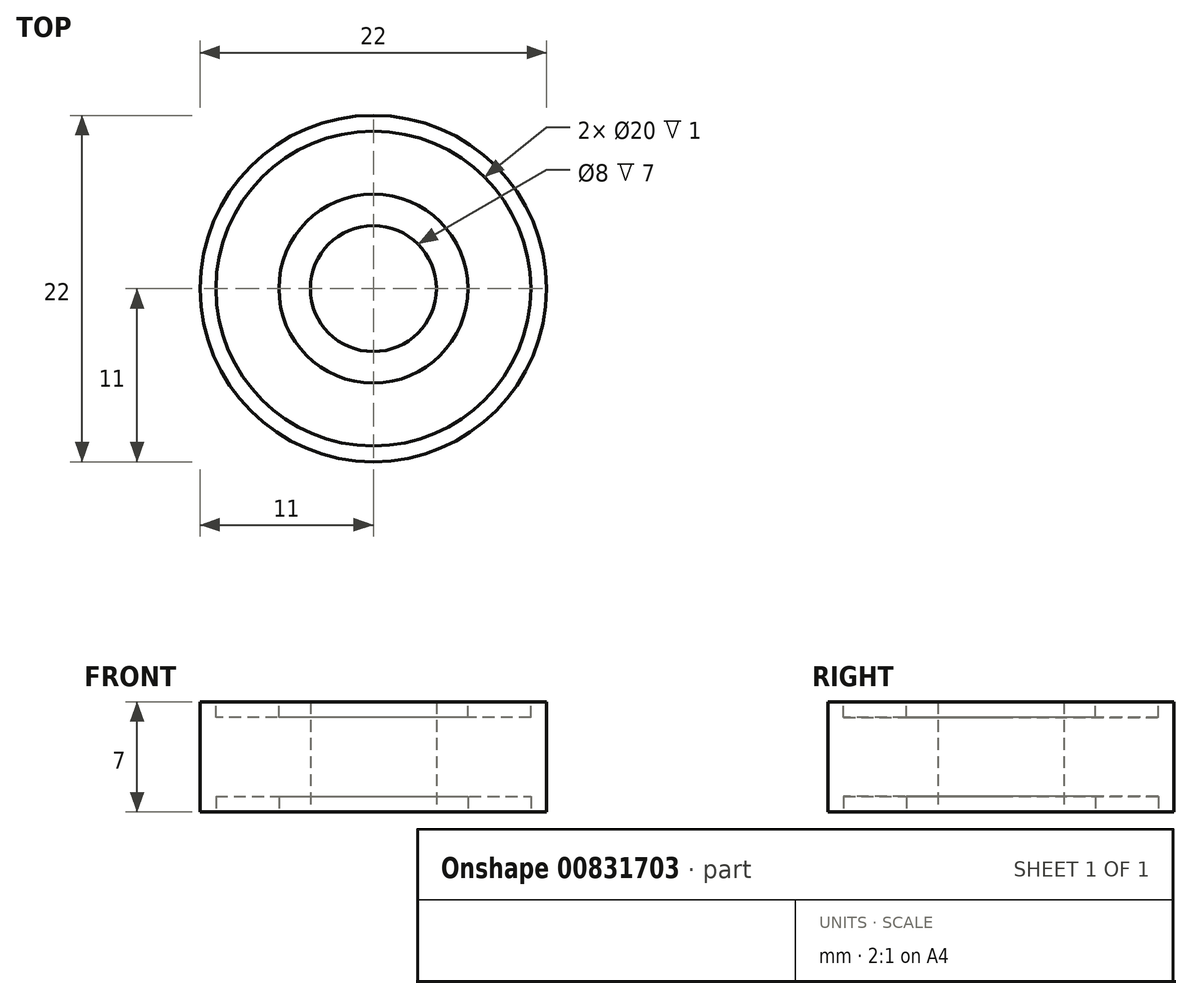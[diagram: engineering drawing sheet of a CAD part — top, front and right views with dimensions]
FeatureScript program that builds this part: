
annotation { "Feature Type Name" : "Feature", "Feature Type Description" : "" }
export const myFeature = defineFeature(function(context is Context, id is Id, definition is map)
    precondition{}
    {
        {
            var Q0;
            Q0=qCreatedBy(makeId("Top.planeOp"),FACE);
            var sketch = newSketch(context, id + "F0", { "sketchPlane" : qUnion([Q0])});
            skCircle(sketch, "E0", {"center": v(0, 0) * mm, "radius": 11 * mm});
            skCircle(sketch, "E1", {"center": v(0, 0) * mm, "radius": 4 * mm});
            skSolve(sketch);
        }
        {
            var Q0;
            Q0=makeQuery(id+"F0.imprint","IMPRINT",FACE,{"disambiguationData":[TD([[makeQuery(id+"F0.imprint","IMPRINT",EDGE,{"derivedFrom":sQuery(id+"F0.wireOp",EDGE,"E0")}),1.0]])]});
            extrude(context, id + "F1", {"entities" : qUnion([Q0]), "depth" : 7 * mm, "offsetDistance" : 25 * mm});
        }
        {
            var Q0;
            Q0=makeQuery(id+"F1.opExtrude","CAP_FACE",FACE,{"disambiguationData":[OSD([sQuery(id+"F0.wireOp",EDGE,"E0"),sQuery(id+"F0.wireOp",EDGE,"E1")])],"isStart":false});
            var sketch = newSketch(context, id + "F2", { "sketchPlane" : qUnion([Q0])});
            skLineSegment(sketch, "E2", {"start": v(-4, 0) * mm, "end": v(-11, 0) * mm});
            skLineSegment(sketch, "E3", {"start": v(4, 0) * mm, "end": v(11, 0) * mm});
            skSolve(sketch);
        }
        {
            var Q0;
            Q0=makeQuery(id+"F1.opExtrude","CAP_FACE",FACE,{"disambiguationData":[OSD([sQuery(id+"F0.wireOp",EDGE,"E0"),sQuery(id+"F0.wireOp",EDGE,"E1")])],"isStart":true});
            var sketch = newSketch(context, id + "F3", { "sketchPlane" : qUnion([Q0])});
            skLineSegment(sketch, "E4", {"start": v(-11, 0) * mm, "end": v(11, 0) * mm});
            skSolve(sketch);
        }
        {
            var Q0;
            Q0=makeQuery(id+"F1.opExtrude","CAP_FACE",FACE,{"disambiguationData":[OSD([sQuery(id+"F0.wireOp",EDGE,"E0"),sQuery(id+"F0.wireOp",EDGE,"E1")])],"isStart":false});
            var sketch = newSketch(context, id + "F4", { "sketchPlane" : qUnion([Q0])});
            skCircle(sketch, "E5", {"center": v(0, 0) * mm, "radius": 6 * mm});
            skCircle(sketch, "E6", {"center": v(0, 0) * mm, "radius": 10 * mm});
            skSolve(sketch);
        }
        {
            var Q0;
            Q0=makeQuery(id+"F4.imprint","IMPRINT",FACE,{"disambiguationData":[TD([[makeQuery(id+"F4.imprint","IMPRINT",EDGE,{"derivedFrom":sQuery(id+"F4.wireOp",EDGE,"E5")}),-1.0]])]});
            extrude(context, id + "F5", {"entities" : qUnion([Q0]), "operationType" : NewBodyOperationType.REMOVE, "oppositeDirection" : true, "depth" : 1 * mm, "offsetDistance" : 25 * mm});
        }
        {
            var Q0;
            Q0=makeQuery(id+"F1.opExtrude","CAP_FACE",FACE,{"disambiguationData":[OSD([sQuery(id+"F0.wireOp",EDGE,"E0"),sQuery(id+"F0.wireOp",EDGE,"E1")])],"isStart":true});
            var sketch = newSketch(context, id + "F6", { "sketchPlane" : qUnion([Q0])});
            skCircle(sketch, "E7", {"center": v(0, 0) * mm, "radius": 6 * mm});
            skCircle(sketch, "E8", {"center": v(0, 0) * mm, "radius": 10 * mm});
            skSolve(sketch);
        }
        {
            var Q0;
            Q0=makeQuery(id+"F6.imprint","IMPRINT",FACE,{"disambiguationData":[TD([[makeQuery(id+"F6.imprint","IMPRINT",EDGE,{"derivedFrom":sQuery(id+"F6.wireOp",EDGE,"E7")}),-1.0]])]});
            extrude(context, id + "F7", {"entities" : qUnion([Q0]), "operationType" : NewBodyOperationType.REMOVE, "oppositeDirection" : true, "depth" : 1 * mm, "offsetDistance" : 25 * mm});
        }
    });
